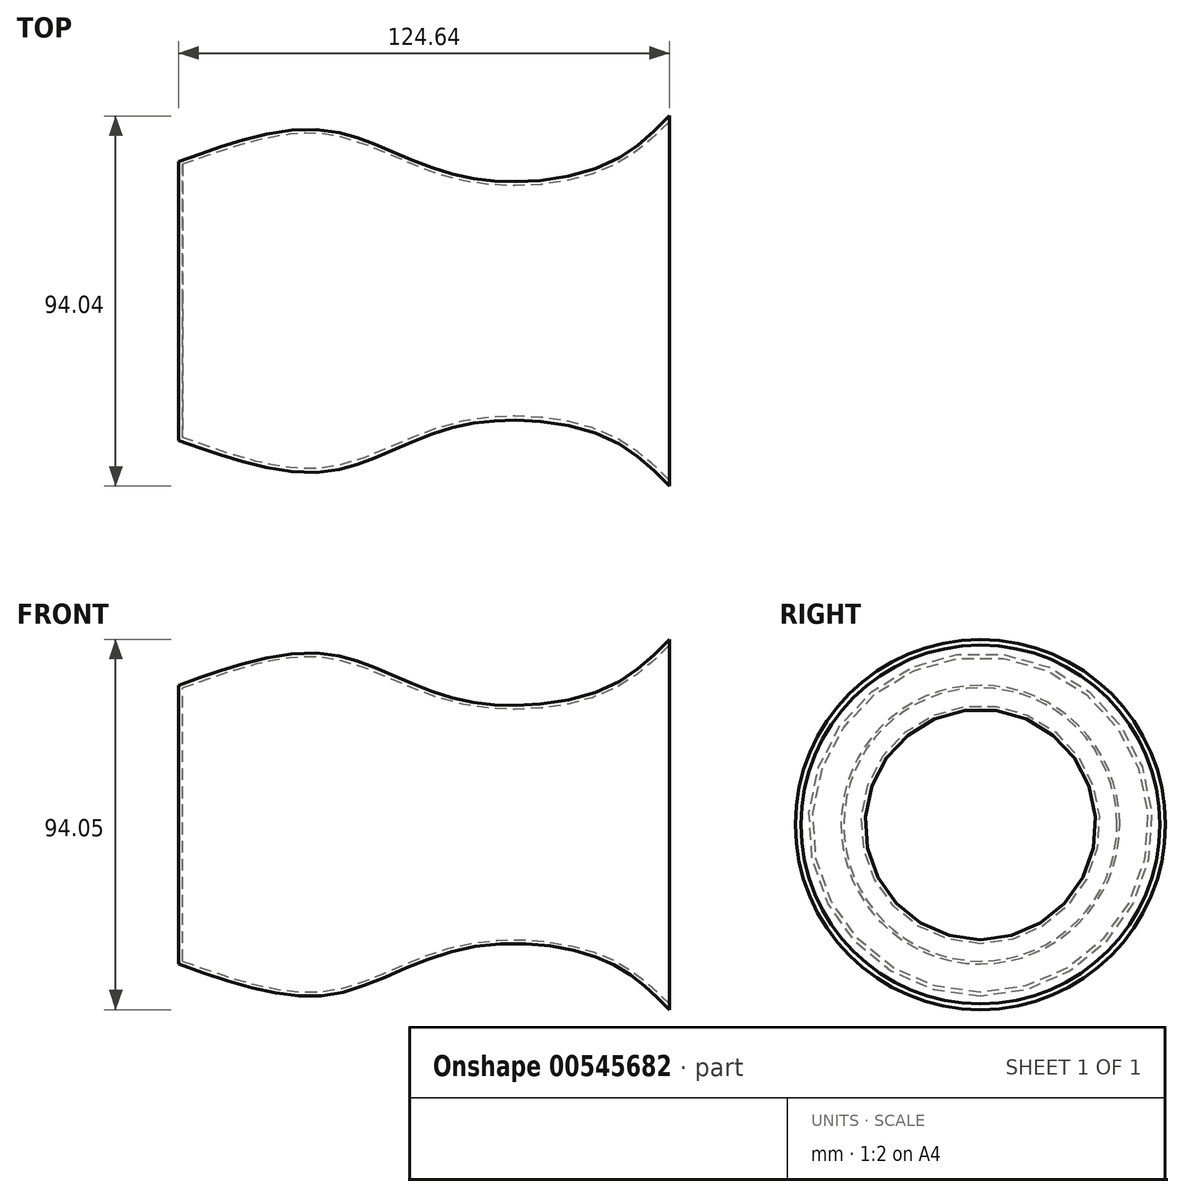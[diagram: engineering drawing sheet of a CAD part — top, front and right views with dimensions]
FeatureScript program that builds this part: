
annotation { "Feature Type Name" : "Feature", "Feature Type Description" : "" }
export const myFeature = defineFeature(function(context is Context, id is Id, definition is map)
    precondition{}
    {
        {
            var Q0;
            Q0=qCreatedBy(makeId("Front.planeOp"),FACE);
            var sketch = newSketch(context, id + "F0", { "sketchPlane" : qUnion([Q0])});
            skFitSpline(sketch, "E0", {"points": [v(-61.75, 43.9) * mm, v(-24.08, 51.84) * mm, v(8.5, 40.5) * mm, v(45.9, 42.77) * mm, v(62.89, 55.52) * mm], "startDerivative": vector(143.84, 51.9) * mm, "endDerivative": vector(70.25, 71.36) * mm});
            skLineSegment(sketch, "E1", {"start": v(62.89, 55.52) * mm, "end": v(62.89, 8.5) * mm});
            skLineSegment(sketch, "E2", {"start": v(62.89, 8.5) * mm, "end": v(-61.75, 8.5) * mm});
            skLineSegment(sketch, "E3", {"start": v(-61.75, 8.5) * mm, "end": v(-61.75, 43.9) * mm});
            skSolve(sketch);
        }
        {
            var Q0;
            Q0=makeQuery(id+"F0.imprint","IMPRINT",FACE,{"disambiguationData":[TD([[makeQuery(id+"F0.imprint","IMPRINT",EDGE,{"derivedFrom":sQuery(id+"F0.wireOp",EDGE,"E0")}),-1.0]])]});
            var Q1;
            Q1=sQuery(id+"F0.wireOp",EDGE,"E2");
            revolve(context, id + "F1", {"entities" : qUnion([Q0]), "axis" : qUnion([Q1]), "revolveType" : RevolveType.FULL});
        }
        {
            var Q0;
            Q0=makeQuery(id+"F1.opRevolve","SWEPT_FACE",FACE,{"disambiguationData":[OSD([sQuery(id+"F0.wireOp",EDGE,"E1")])]});
            shell(context, id + "F2", {"entities" : qUnion([Q0]), "thickness" : 1 * mm});
        }
    });
